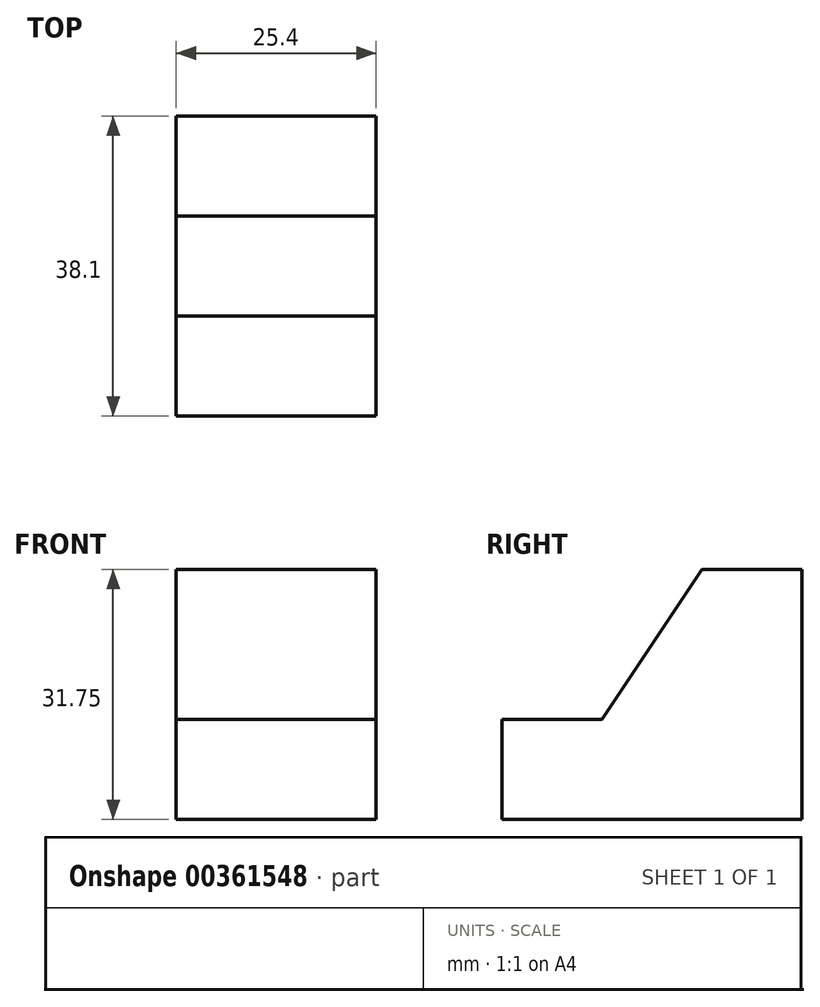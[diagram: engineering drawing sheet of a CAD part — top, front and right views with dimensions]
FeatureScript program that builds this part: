
annotation { "Feature Type Name" : "Feature", "Feature Type Description" : "" }
export const myFeature = defineFeature(function(context is Context, id is Id, definition is map)
    precondition{}
    {
        {
            var Q0;
            Q0=qCreatedBy(makeId("Right.planeOp"),FACE);
            var sketch = newSketch(context, id + "F0", { "sketchPlane" : qUnion([Q0])});
            skLineSegment(sketch, "E0", {"start": v(0, 31.75) * mm, "end": v(-12.7, 31.75) * mm});
            skLineSegment(sketch, "E1", {"start": v(-12.7, 31.75) * mm, "end": v(-25.4, 12.7) * mm});
            skLineSegment(sketch, "E2", {"start": v(-25.4, 12.7) * mm, "end": v(-38.1, 12.7) * mm});
            skLineSegment(sketch, "E3", {"start": v(0, 31.75) * mm, "end": v(0, 0) * mm});
            skLineSegment(sketch, "E4", {"start": v(-38.1, 12.7) * mm, "end": v(-38.1, 0) * mm});
            skLineSegment(sketch, "E5", {"start": v(-38.1, 0) * mm, "end": v(0, 0) * mm});
            skSolve(sketch);
        }
        {
            var Q0;
            Q0=makeQuery(id+"F0.imprint","IMPRINT",FACE,{"disambiguationData":[TD([[makeQuery(id+"F0.imprint","IMPRINT",EDGE,{"derivedFrom":sQuery(id+"F0.wireOp",EDGE,"E0")}),1.0]])]});
            extrude(context, id + "F1", {"entities" : qUnion([Q0]), "depth" : 25.4 * mm});
        }
    });
